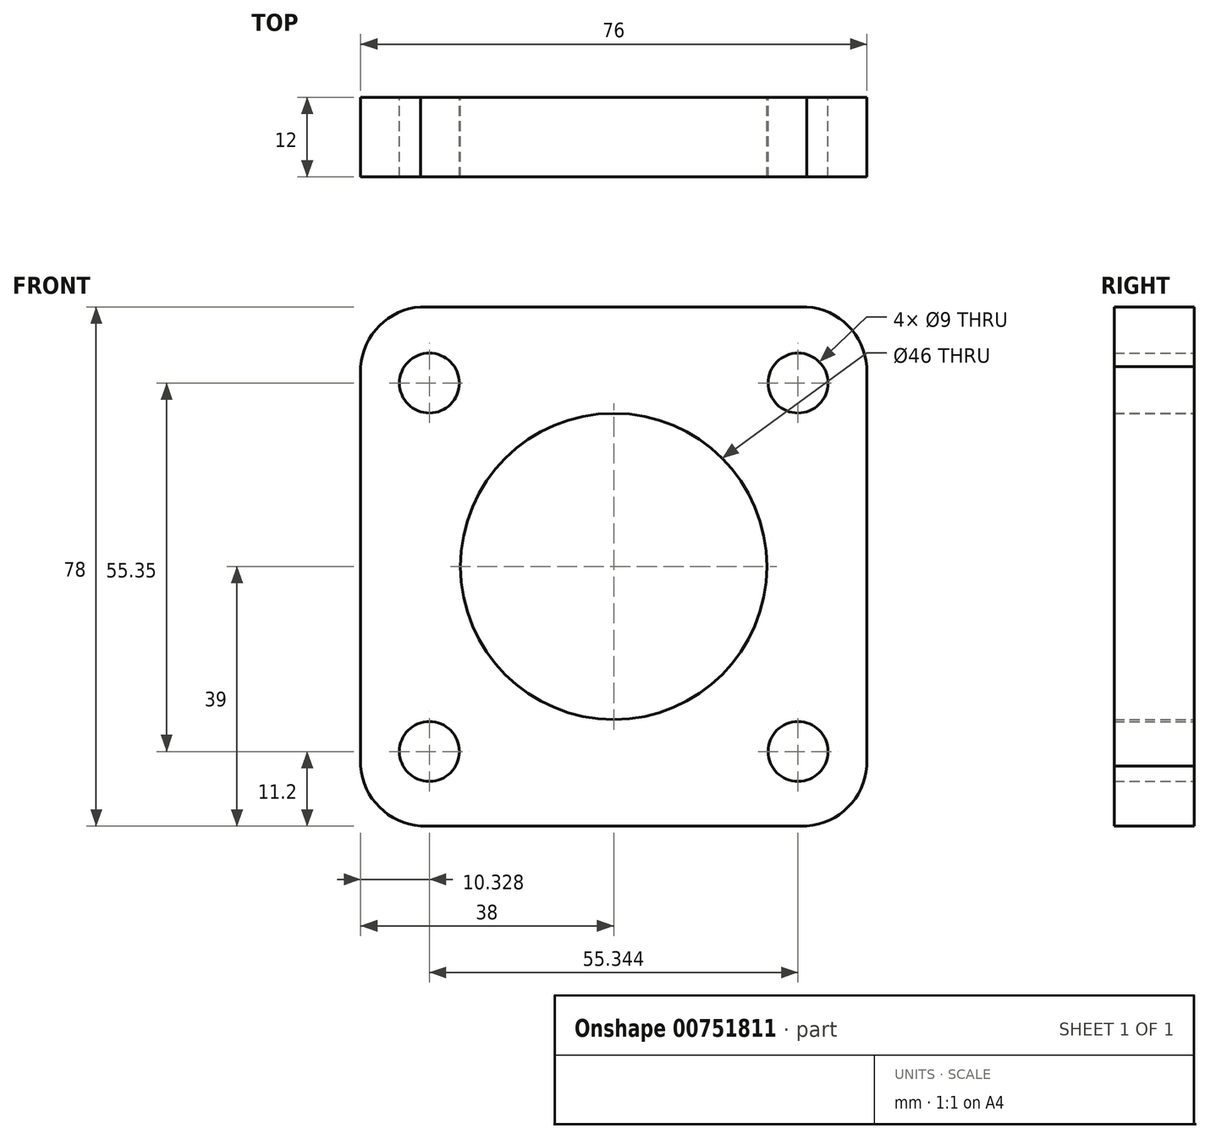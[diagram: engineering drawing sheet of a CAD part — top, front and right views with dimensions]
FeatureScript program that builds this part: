
annotation { "Feature Type Name" : "Feature", "Feature Type Description" : "" }
export const myFeature = defineFeature(function(context is Context, id is Id, definition is map)
    precondition{}
    {
        {
            var Q0;
            Q0=qCreatedBy(makeId("Front.planeOp"),FACE);
            var sketch = newSketch(context, id + "F0", { "sketchPlane" : qUnion([Q0])});
            skLineSegment(sketch, "E0.bottom", {"start": v(38, 39) * mm, "end": v(-38, 39) * mm});
            skLineSegment(sketch, "E0.top", {"start": v(38, -39) * mm, "end": v(-38, -39) * mm});
            skLineSegment(sketch, "E0.left", {"start": v(38, 39) * mm, "end": v(38, -39) * mm});
            skLineSegment(sketch, "E0.right", {"start": v(-38, 39) * mm, "end": v(-38, -39) * mm});
            skPoint(sketch, "E0.middle", {"position": v(0, 0) * mm});
            skCircle(sketch, "E1", {"center": v(0, 0) * mm, "radius": 23 * mm});
            skCircle(sketch, "E2", {"center": v(-27.67, 27.55) * mm, "radius": 4.5 * mm});
            skCircle(sketch, "E3", {"center": v(27.67, 27.55) * mm, "radius": 4.5 * mm});
            skCircle(sketch, "E4", {"center": v(-27.67, -27.8) * mm, "radius": 4.5 * mm});
            skCircle(sketch, "E5", {"center": v(27.67, -27.8) * mm, "radius": 4.5 * mm});
            skArc(sketch, "E6", {"start": v(38, 30) * mm, "mid": v(35.17, 36.17) * mm, "end": v(29, 39) * mm});
            skArc(sketch, "E7", {"start": v(-29, 39) * mm, "mid": v(-35.17, 36.17) * mm, "end": v(-38, 30) * mm});
            skArc(sketch, "E8", {"start": v(29, -39) * mm, "mid": v(35.17, -36.17) * mm, "end": v(38, -30) * mm});
            skArc(sketch, "E9", {"start": v(-38, -30) * mm, "mid": v(-35.17, -36.17) * mm, "end": v(-29, -39) * mm});
            skSolve(sketch);
        }
        {
            var Q0;
            Q0=makeQuery(id+"F0.imprint","IMPRINT",FACE,{"disambiguationData":[TD([[makeQuery(id+"F0.imprint","IMPRINT",EDGE,{"derivedFrom":sQuery(id+"F0.wireOp",EDGE,"E1")}),-1.0]])]});
            extrude(context, id + "F1", {"entities" : qUnion([Q0]), "depth" : 12 * mm, "offsetDistance" : 25 * mm});
        }
    });
